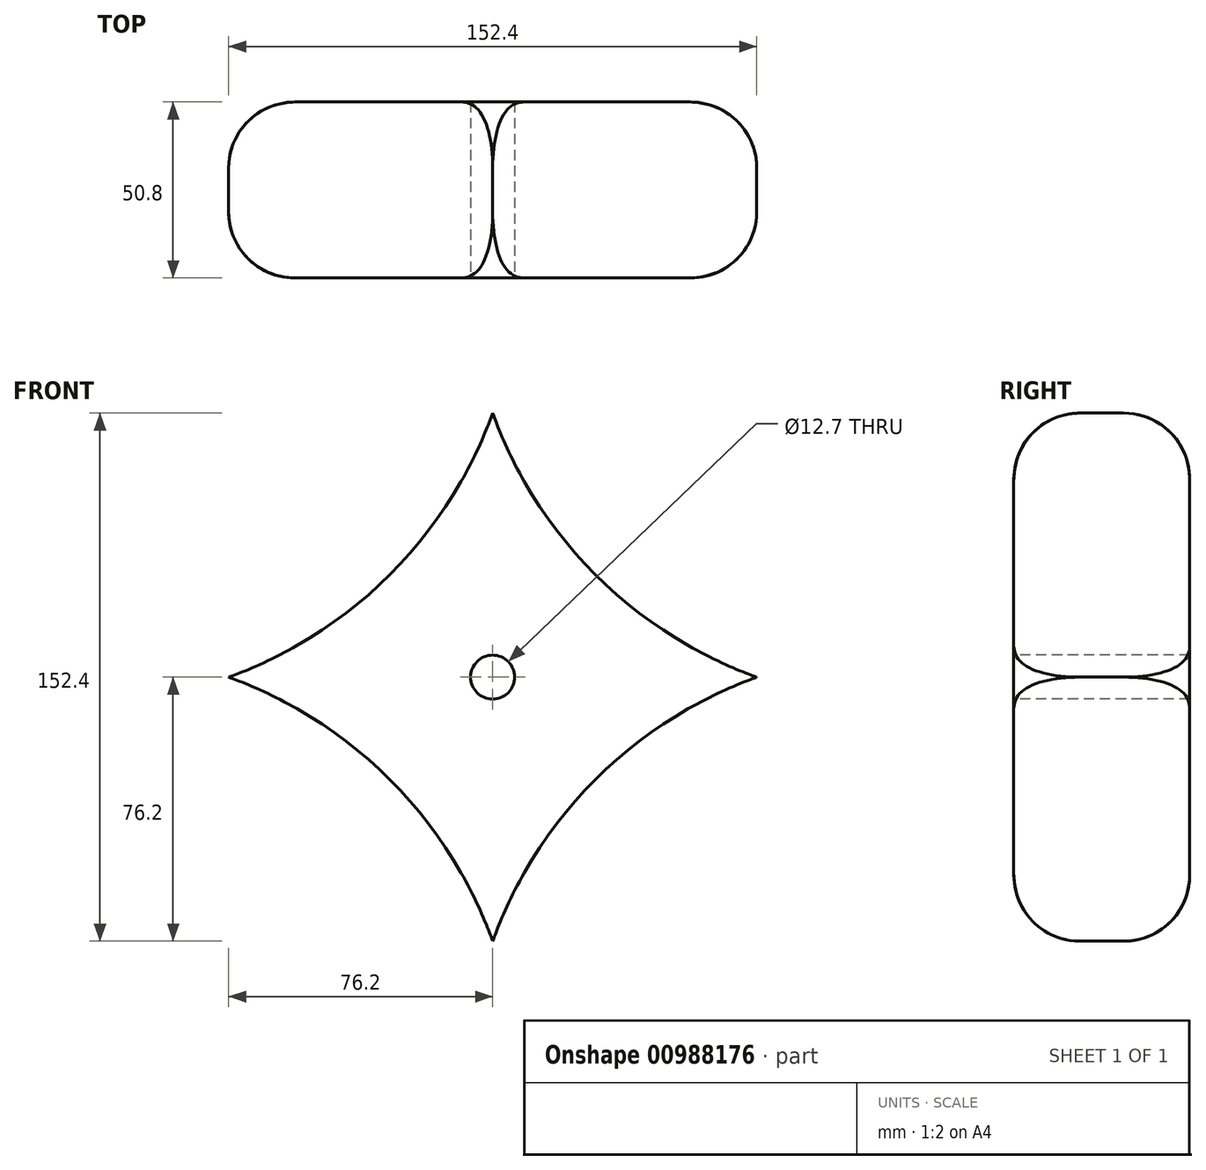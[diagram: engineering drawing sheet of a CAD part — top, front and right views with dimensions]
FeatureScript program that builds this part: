
annotation { "Feature Type Name" : "Feature", "Feature Type Description" : "" }
export const myFeature = defineFeature(function(context is Context, id is Id, definition is map)
    precondition{}
    {
        {
            var Q0;
            Q0=qCreatedBy(makeId("Front.planeOp"),FACE);
            var sketch = newSketch(context, id + "F0", { "sketchPlane" : qUnion([Q0])});
            skCircle(sketch, "E0", {"center": v(0, 0) * mm, "radius": 76.2 * mm});
            skSolve(sketch);
        }
        {
            var Q0;
            Q0 = qSketchRegion(id + "F0", true);
            extrude(context, id + "F1", {"entities" : qUnion([Q0]), "depth" : 50.8 * mm, "offsetDistance" : 25.4 * mm});
        }
        {
            var Q0;
            Q0=makeQuery(id+"F1.opExtrude","CAP_FACE",FACE,{"disambiguationData":[OSD([sQuery(id+"F0.wireOp",EDGE,"E0")])],"isStart":false});
            var sketch = newSketch(context, id + "F2", { "sketchPlane" : qUnion([Q0])});
            skLineSegment(sketch, "E1.bottom", {"start": v(76.2, 76.2) * mm, "end": v(-76.2, 76.2) * mm});
            skLineSegment(sketch, "E1.top", {"start": v(76.2, -76.2) * mm, "end": v(-76.2, -76.2) * mm});
            skLineSegment(sketch, "E1.left", {"start": v(76.2, 76.2) * mm, "end": v(76.2, -76.2) * mm});
            skLineSegment(sketch, "E1.right", {"start": v(-76.2, 76.2) * mm, "end": v(-76.2, -76.2) * mm});
            skPoint(sketch, "E1.middle", {"position": v(0, 0) * mm});
            skLineSegment(sketch, "E2", {"start": v(-76.2, 76.2) * mm, "end": v(76.2, -76.2) * mm});
            skLineSegment(sketch, "E3", {"start": v(76.2, 76.2) * mm, "end": v(-76.2, -76.2) * mm});
            skLineSegment(sketch, "E4", {"start": v(0, -76.2) * mm, "end": v(76.2, 0) * mm});
            skLineSegment(sketch, "E5", {"start": v(76.2, 0) * mm, "end": v(0, 76.2) * mm});
            skLineSegment(sketch, "E6", {"start": v(0, 76.2) * mm, "end": v(-76.2, 0) * mm});
            skLineSegment(sketch, "E7", {"start": v(-76.2, 0) * mm, "end": v(0, -76.2) * mm});
            skArc(sketch, "E8", {"start": v(0, -76.2) * mm, "mid": v(-29.62, -29.62) * mm, "end": v(-76.2, 0) * mm});
            skArc(sketch, "E9", {"start": v(76.2, 0) * mm, "mid": v(29.62, -29.62) * mm, "end": v(0, -76.2) * mm});
            skArc(sketch, "E10", {"start": v(0, 76.2) * mm, "mid": v(29.62, 29.62) * mm, "end": v(76.2, 0) * mm});
            skArc(sketch, "E11", {"start": v(-76.2, 0) * mm, "mid": v(-29.62, 29.62) * mm, "end": v(0, 76.2) * mm});
            skSolve(sketch);
        }
        {
            var Q0;
            Q0=makeQuery(id+"F1.opExtrude","SWEPT_FACE",FACE,{"disambiguationData":[OSD([sQuery(id+"F0.wireOp",EDGE,"E0")])]});
            fillet(context, id + "F3", {"entities" : qUnion([Q0]), "radius" : 19.05 * mm, "tangentPropagation" : true, "allowEdgeOverflow" : false});
        }
        {
            var Q0;
            {var subQ0=sQuery(id+"F2.wireOp",EDGE,"E6");var subQ1=sQuery(id+"F2.wireOp",EDGE,"E2");var subQ2=makeQuery(id+"F2.imprint","INTERSECT",VERTEX,{"derivedFrom":[subQ1,subQ0]});Q0=makeQuery(id+"F2.imprint","IMPRINT",FACE,{"disambiguationData":[TD([[makeQuery(id+"F2.imprint","IMPRINT",EDGE,{"disambiguationData":[TD([[subQ2,-1.0]])],"derivedFrom":subQ1}),1.0]])]});}
            var Q1;
            {var subQ0=sQuery(id+"F2.wireOp",EDGE,"E6");var subQ1=sQuery(id+"F2.wireOp",EDGE,"E2");var subQ2=makeQuery(id+"F2.imprint","INTERSECT",VERTEX,{"derivedFrom":[subQ1,subQ0]});Q1=makeQuery(id+"F2.imprint","IMPRINT",FACE,{"disambiguationData":[TD([[makeQuery(id+"F2.imprint","IMPRINT",EDGE,{"disambiguationData":[TD([[subQ2,-1.0]])],"derivedFrom":subQ1}),-1.0]])]});}
            var Q2;
            {var subQ0=sQuery(id+"F2.wireOp",EDGE,"E9");var subQ1=sQuery(id+"F2.wireOp",EDGE,"E2");var subQ2=makeQuery(id+"F2.imprint","INTERSECT",VERTEX,{"derivedFrom":[subQ1,subQ0]});Q2=makeQuery(id+"F2.imprint","IMPRINT",FACE,{"disambiguationData":[TD([[makeQuery(id+"F2.imprint","IMPRINT",EDGE,{"disambiguationData":[TD([[subQ2,-1.0]])],"derivedFrom":subQ1}),-1.0]])]});}
            var Q3;
            {var subQ0=sQuery(id+"F2.wireOp",EDGE,"E9");var subQ1=sQuery(id+"F2.wireOp",EDGE,"E2");var subQ2=makeQuery(id+"F2.imprint","INTERSECT",VERTEX,{"derivedFrom":[subQ1,subQ0]});Q3=makeQuery(id+"F2.imprint","IMPRINT",FACE,{"disambiguationData":[TD([[makeQuery(id+"F2.imprint","IMPRINT",EDGE,{"disambiguationData":[TD([[subQ2,-1.0]])],"derivedFrom":subQ1}),1.0]])]});}
            var Q4;
            {var subQ0=sQuery(id+"F2.wireOp",EDGE,"E5");var subQ1=sQuery(id+"F2.wireOp",EDGE,"E3");var subQ2=makeQuery(id+"F2.imprint","INTERSECT",VERTEX,{"derivedFrom":[subQ1,subQ0]});Q4=makeQuery(id+"F2.imprint","IMPRINT",FACE,{"disambiguationData":[TD([[makeQuery(id+"F2.imprint","IMPRINT",EDGE,{"disambiguationData":[TD([[subQ2,-1.0]])],"derivedFrom":subQ1}),1.0]])]});}
            var Q5;
            {var subQ0=sQuery(id+"F2.wireOp",EDGE,"E5");var subQ1=sQuery(id+"F2.wireOp",EDGE,"E3");var subQ2=makeQuery(id+"F2.imprint","INTERSECT",VERTEX,{"derivedFrom":[subQ1,subQ0]});Q5=makeQuery(id+"F2.imprint","IMPRINT",FACE,{"disambiguationData":[TD([[makeQuery(id+"F2.imprint","IMPRINT",EDGE,{"disambiguationData":[TD([[subQ2,-1.0]])],"derivedFrom":subQ1}),-1.0]])]});}
            var Q6;
            {var subQ0=sQuery(id+"F2.wireOp",EDGE,"E8");var subQ1=sQuery(id+"F2.wireOp",EDGE,"E3");var subQ2=makeQuery(id+"F2.imprint","INTERSECT",VERTEX,{"derivedFrom":[subQ1,subQ0]});Q6=makeQuery(id+"F2.imprint","IMPRINT",FACE,{"disambiguationData":[TD([[makeQuery(id+"F2.imprint","IMPRINT",EDGE,{"disambiguationData":[TD([[subQ2,-1.0]])],"derivedFrom":subQ1}),-1.0]])]});}
            var Q7;
            {var subQ0=sQuery(id+"F2.wireOp",EDGE,"E8");var subQ1=sQuery(id+"F2.wireOp",EDGE,"E3");var subQ2=makeQuery(id+"F2.imprint","INTERSECT",VERTEX,{"derivedFrom":[subQ1,subQ0]});Q7=makeQuery(id+"F2.imprint","IMPRINT",FACE,{"disambiguationData":[TD([[makeQuery(id+"F2.imprint","IMPRINT",EDGE,{"disambiguationData":[TD([[subQ2,-1.0]])],"derivedFrom":subQ1}),1.0]])]});}
            var Q8;
            {var subQ0=sQuery(id+"F2.wireOp",EDGE,"E3");var subQ3=makeQuery(id+"F1.opExtrude","CAP_EDGE",EDGE,{"disambiguationData":[OSD([sQuery(id+"F0.wireOp",EDGE,"E0")])],"isStart":false});var subQ5=makeQuery(id+"F2.imprint","INTERSECT",VERTEX,{"disambiguationData":[OD(0.0)],"derivedFrom":[subQ3,subQ0]});Q8=makeQuery(id+"F2.imprint","IMPRINT",FACE,{"disambiguationData":[TD([[makeQuery(id+"F2.imprint","IMPRINT",EDGE,{"disambiguationData":[TD([[subQ5,1.0]])],"derivedFrom":subQ0}),-1.0]])]});}
            var Q9;
            {var subQ0=sQuery(id+"F2.wireOp",EDGE,"E2");var subQ3=makeQuery(id+"F1.opExtrude","CAP_EDGE",EDGE,{"disambiguationData":[OSD([sQuery(id+"F0.wireOp",EDGE,"E0")])],"isStart":false});var subQ5=makeQuery(id+"F2.imprint","INTERSECT",VERTEX,{"disambiguationData":[OD(0.0)],"derivedFrom":[subQ3,subQ0]});Q9=makeQuery(id+"F2.imprint","IMPRINT",FACE,{"disambiguationData":[TD([[makeQuery(id+"F2.imprint","IMPRINT",EDGE,{"disambiguationData":[TD([[subQ5,1.0]])],"derivedFrom":subQ0}),1.0]])]});}
            var Q10;
            {var subQ0=sQuery(id+"F2.wireOp",EDGE,"E2");var subQ3=makeQuery(id+"F1.opExtrude","CAP_EDGE",EDGE,{"disambiguationData":[OSD([sQuery(id+"F0.wireOp",EDGE,"E0")])],"isStart":false});var subQ5=makeQuery(id+"F2.imprint","INTERSECT",VERTEX,{"disambiguationData":[OD(1.0)],"derivedFrom":[subQ3,subQ0]});Q10=makeQuery(id+"F2.imprint","IMPRINT",FACE,{"disambiguationData":[TD([[makeQuery(id+"F2.imprint","IMPRINT",EDGE,{"disambiguationData":[TD([[subQ5,-1.0]])],"derivedFrom":subQ0}),-1.0]])]});}
            var Q11;
            {var subQ0=sQuery(id+"F2.wireOp",EDGE,"E3");var subQ3=makeQuery(id+"F1.opExtrude","CAP_EDGE",EDGE,{"disambiguationData":[OSD([sQuery(id+"F0.wireOp",EDGE,"E0")])],"isStart":false});var subQ5=makeQuery(id+"F2.imprint","INTERSECT",VERTEX,{"disambiguationData":[OD(1.0)],"derivedFrom":[subQ3,subQ0]});Q11=makeQuery(id+"F2.imprint","IMPRINT",FACE,{"disambiguationData":[TD([[makeQuery(id+"F2.imprint","IMPRINT",EDGE,{"disambiguationData":[TD([[subQ5,-1.0]])],"derivedFrom":subQ0}),1.0]])]});}
            var Q12;
            {var subQ0=sQuery(id+"F2.wireOp",EDGE,"E3");var subQ3=makeQuery(id+"F1.opExtrude","CAP_EDGE",EDGE,{"disambiguationData":[OSD([sQuery(id+"F0.wireOp",EDGE,"E0")])],"isStart":false});var subQ5=makeQuery(id+"F2.imprint","INTERSECT",VERTEX,{"disambiguationData":[OD(0.0)],"derivedFrom":[subQ3,subQ0]});Q12=makeQuery(id+"F2.imprint","IMPRINT",FACE,{"disambiguationData":[TD([[makeQuery(id+"F2.imprint","IMPRINT",EDGE,{"disambiguationData":[TD([[subQ5,1.0]])],"derivedFrom":subQ0}),1.0]])]});}
            var Q13;
            {var subQ0=sQuery(id+"F2.wireOp",EDGE,"E2");var subQ3=makeQuery(id+"F1.opExtrude","CAP_EDGE",EDGE,{"disambiguationData":[OSD([sQuery(id+"F0.wireOp",EDGE,"E0")])],"isStart":false});var subQ5=makeQuery(id+"F2.imprint","INTERSECT",VERTEX,{"disambiguationData":[OD(1.0)],"derivedFrom":[subQ3,subQ0]});Q13=makeQuery(id+"F2.imprint","IMPRINT",FACE,{"disambiguationData":[TD([[makeQuery(id+"F2.imprint","IMPRINT",EDGE,{"disambiguationData":[TD([[subQ5,-1.0]])],"derivedFrom":subQ0}),1.0]])]});}
            var Q14;
            {var subQ0=sQuery(id+"F2.wireOp",EDGE,"E2");var subQ3=makeQuery(id+"F1.opExtrude","CAP_EDGE",EDGE,{"disambiguationData":[OSD([sQuery(id+"F0.wireOp",EDGE,"E0")])],"isStart":false});var subQ5=makeQuery(id+"F2.imprint","INTERSECT",VERTEX,{"disambiguationData":[OD(0.0)],"derivedFrom":[subQ3,subQ0]});Q14=makeQuery(id+"F2.imprint","IMPRINT",FACE,{"disambiguationData":[TD([[makeQuery(id+"F2.imprint","IMPRINT",EDGE,{"disambiguationData":[TD([[subQ5,1.0]])],"derivedFrom":subQ0}),-1.0]])]});}
            var Q15;
            {var subQ0=sQuery(id+"F2.wireOp",EDGE,"E3");var subQ3=makeQuery(id+"F1.opExtrude","CAP_EDGE",EDGE,{"disambiguationData":[OSD([sQuery(id+"F0.wireOp",EDGE,"E0")])],"isStart":false});var subQ5=makeQuery(id+"F2.imprint","INTERSECT",VERTEX,{"disambiguationData":[OD(1.0)],"derivedFrom":[subQ3,subQ0]});Q15=makeQuery(id+"F2.imprint","IMPRINT",FACE,{"disambiguationData":[TD([[makeQuery(id+"F2.imprint","IMPRINT",EDGE,{"disambiguationData":[TD([[subQ5,-1.0]])],"derivedFrom":subQ0}),-1.0]])]});}
            var Q16;
            {var subQ0=sQuery(id+"F2.wireOp",EDGE,"E6");var subQ1=sQuery(id+"F2.wireOp",EDGE,"E2");var subQ2=makeQuery(id+"F2.imprint","INTERSECT",VERTEX,{"derivedFrom":[subQ1,subQ0]});Q16=makeQuery(id+"F2.imprint","IMPRINT",FACE,{"disambiguationData":[TD([[makeQuery(id+"F2.imprint","IMPRINT",EDGE,{"disambiguationData":[TD([[subQ2,1.0]])],"derivedFrom":subQ1}),1.0]])]});}
            var Q17;
            {var subQ0=sQuery(id+"F2.wireOp",EDGE,"E6");var subQ1=sQuery(id+"F2.wireOp",EDGE,"E2");var subQ2=makeQuery(id+"F2.imprint","INTERSECT",VERTEX,{"derivedFrom":[subQ1,subQ0]});Q17=makeQuery(id+"F2.imprint","IMPRINT",FACE,{"disambiguationData":[TD([[makeQuery(id+"F2.imprint","IMPRINT",EDGE,{"disambiguationData":[TD([[subQ2,1.0]])],"derivedFrom":subQ1}),-1.0]])]});}
            var Q18;
            {var subQ0=sQuery(id+"F2.wireOp",EDGE,"E4");var subQ1=sQuery(id+"F2.wireOp",EDGE,"E2");var subQ2=makeQuery(id+"F2.imprint","INTERSECT",VERTEX,{"derivedFrom":[subQ1,subQ0]});Q18=makeQuery(id+"F2.imprint","IMPRINT",FACE,{"disambiguationData":[TD([[makeQuery(id+"F2.imprint","IMPRINT",EDGE,{"disambiguationData":[TD([[subQ2,-1.0]])],"derivedFrom":subQ1}),-1.0]])]});}
            var Q19;
            {var subQ0=sQuery(id+"F2.wireOp",EDGE,"E4");var subQ1=sQuery(id+"F2.wireOp",EDGE,"E2");var subQ2=makeQuery(id+"F2.imprint","INTERSECT",VERTEX,{"derivedFrom":[subQ1,subQ0]});Q19=makeQuery(id+"F2.imprint","IMPRINT",FACE,{"disambiguationData":[TD([[makeQuery(id+"F2.imprint","IMPRINT",EDGE,{"disambiguationData":[TD([[subQ2,-1.0]])],"derivedFrom":subQ1}),1.0]])]});}
            var Q20;
            {var subQ0=sQuery(id+"F2.wireOp",EDGE,"E5");var subQ1=sQuery(id+"F2.wireOp",EDGE,"E3");var subQ2=makeQuery(id+"F2.imprint","INTERSECT",VERTEX,{"derivedFrom":[subQ1,subQ0]});Q20=makeQuery(id+"F2.imprint","IMPRINT",FACE,{"disambiguationData":[TD([[makeQuery(id+"F2.imprint","IMPRINT",EDGE,{"disambiguationData":[TD([[subQ2,1.0]])],"derivedFrom":subQ1}),1.0]])]});}
            var Q21;
            {var subQ0=sQuery(id+"F2.wireOp",EDGE,"E5");var subQ1=sQuery(id+"F2.wireOp",EDGE,"E3");var subQ2=makeQuery(id+"F2.imprint","INTERSECT",VERTEX,{"derivedFrom":[subQ1,subQ0]});Q21=makeQuery(id+"F2.imprint","IMPRINT",FACE,{"disambiguationData":[TD([[makeQuery(id+"F2.imprint","IMPRINT",EDGE,{"disambiguationData":[TD([[subQ2,1.0]])],"derivedFrom":subQ1}),-1.0]])]});}
            var Q22;
            {var subQ0=sQuery(id+"F2.wireOp",EDGE,"E7");var subQ1=sQuery(id+"F2.wireOp",EDGE,"E3");var subQ2=makeQuery(id+"F2.imprint","INTERSECT",VERTEX,{"derivedFrom":[subQ1,subQ0]});Q22=makeQuery(id+"F2.imprint","IMPRINT",FACE,{"disambiguationData":[TD([[makeQuery(id+"F2.imprint","IMPRINT",EDGE,{"disambiguationData":[TD([[subQ2,-1.0]])],"derivedFrom":subQ1}),-1.0]])]});}
            var Q23;
            {var subQ0=sQuery(id+"F2.wireOp",EDGE,"E7");var subQ1=sQuery(id+"F2.wireOp",EDGE,"E3");var subQ2=makeQuery(id+"F2.imprint","INTERSECT",VERTEX,{"derivedFrom":[subQ1,subQ0]});Q23=makeQuery(id+"F2.imprint","IMPRINT",FACE,{"disambiguationData":[TD([[makeQuery(id+"F2.imprint","IMPRINT",EDGE,{"disambiguationData":[TD([[subQ2,-1.0]])],"derivedFrom":subQ1}),1.0]])]});}
            extrude(context, id + "F4", {"entities" : qUnion([Q0, Q1, Q2, Q3, Q4, Q5, Q6, Q7, Q8, Q9, Q10, Q11, Q12, Q13, Q14, Q15, Q16, Q17, Q18, Q19, Q20, Q21, Q22, Q23]), "operationType" : NewBodyOperationType.REMOVE, "endBound" : BoundingType.THROUGH_ALL, "oppositeDirection" : true, "depth" : 25.4 * mm, "offsetDistance" : 25.4 * mm});
        }
        {
            var Q0;
            Q0=makeQuery(id+"F1.opExtrude","CAP_FACE",FACE,{"disambiguationData":[OSD([sQuery(id+"F0.wireOp",EDGE,"E0")])],"isStart":false});
            var sketch = newSketch(context, id + "F5", { "sketchPlane" : qUnion([Q0])});
            skCircle(sketch, "E12", {"center": v(0, 0) * mm, "radius": 6.35 * mm});
            skSolve(sketch);
        }
        {
            var Q0;
            Q0 = qSketchRegion(id + "F5", true);
            extrude(context, id + "F6", {"entities" : qUnion([Q0]), "operationType" : NewBodyOperationType.REMOVE, "endBound" : BoundingType.THROUGH_ALL, "oppositeDirection" : true, "depth" : 25.4 * mm, "offsetDistance" : 25.4 * mm});
        }
    });
